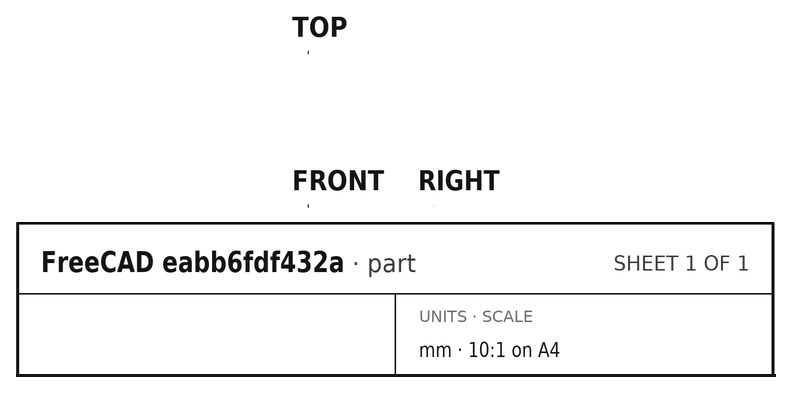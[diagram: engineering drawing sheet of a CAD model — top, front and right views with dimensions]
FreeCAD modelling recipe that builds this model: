
FCSTD DOCUMENT  (FreeCAD 0.21R33694 (Git))
Label: Lee_microstrip
License: All rights reserved
LicenseURL: http://en.wikipedia.org/wiki/All_rights_reserved
objects: Part::Part2DObjectPython×4, Part::Cut×1, Part::FeaturePython×1, App::FeaturePython×1
note: 6 computed .brp shape members not serialized (recipe doc carries the construction recipe); baked Part::Feature solids carry a one-line shape summary decoded from their .brp

FEATURE [Part::Part2DObjectPython] Rectangle004  label="Lee_semiconductor"  # Draft 2D object (typed FeaturePython)
  Area = 6.25e-07
  ChamferSize = 0
  Columns = 1
  FilletRadius = 0
  Height = 0.00025
  Length = 0.0025
  MakeFace = true
  Rows = 1
FEATURE [Part::Part2DObjectPython] Rectangle005  label="strip001"  # Draft 2D object (typed FeaturePython)
  Area = 1.25e-08
  ChamferSize = 0
  Columns = 1
  FilletRadius = 0
  Height = 5e-05
  Length = 0.00025
  MakeFace = true
  Placement = pos=(0.001125,0.00025,0) rot=(0,0,1;0rad)
  Rows = 1
FEATURE [Part::Part2DObjectPython] Rectangle006  label="air001"  # Draft 2D object (typed FeaturePython)
  Area = 5.625e-06
  ChamferSize = 0
  Columns = 1
  FilletRadius = 0
  Height = 0.00225
  Length = 0.0025
  MakeFace = true
  Placement = pos=(0,0.00025,0) rot=(0,0,1;0rad)
  Rows = 1
FEATURE [Part::Cut] Cut001  label="air002"
  Base = -> Rectangle006
  Tool = -> Rectangle005
FEATURE [Part::FeaturePython] BooleanFragments001  label="Lee_microstrip"  # WARN: FeaturePython — macro-defined, semantics opaque (R4)
  Mode = 0
  Objects = -> [Rectangle004,Cut001]
  Tolerance = 0
FEATURE [Part::Part2DObjectPython] Rectangle  label="_Pline1"  # Draft 2D object (typed FeaturePython)
  Area = 0
  ChamferSize = 0
  Columns = 1
  FilletRadius = 0
  Height = 5e-05
  Length = 0.00025
  MakeFace = false
  Placement = pos=(0.001125,0.00025,0) rot=(0,0,1;0rad)
  Rows = 1
FEATURE [App::FeaturePython] Text001  label="_L1(current){line1}"  # WARN: FeaturePython — macro-defined, semantics opaque (R4)
  Placement = pos=(0.00123975,-0.000526531,0) rot=(0,0,1;0rad)
  Text = .
